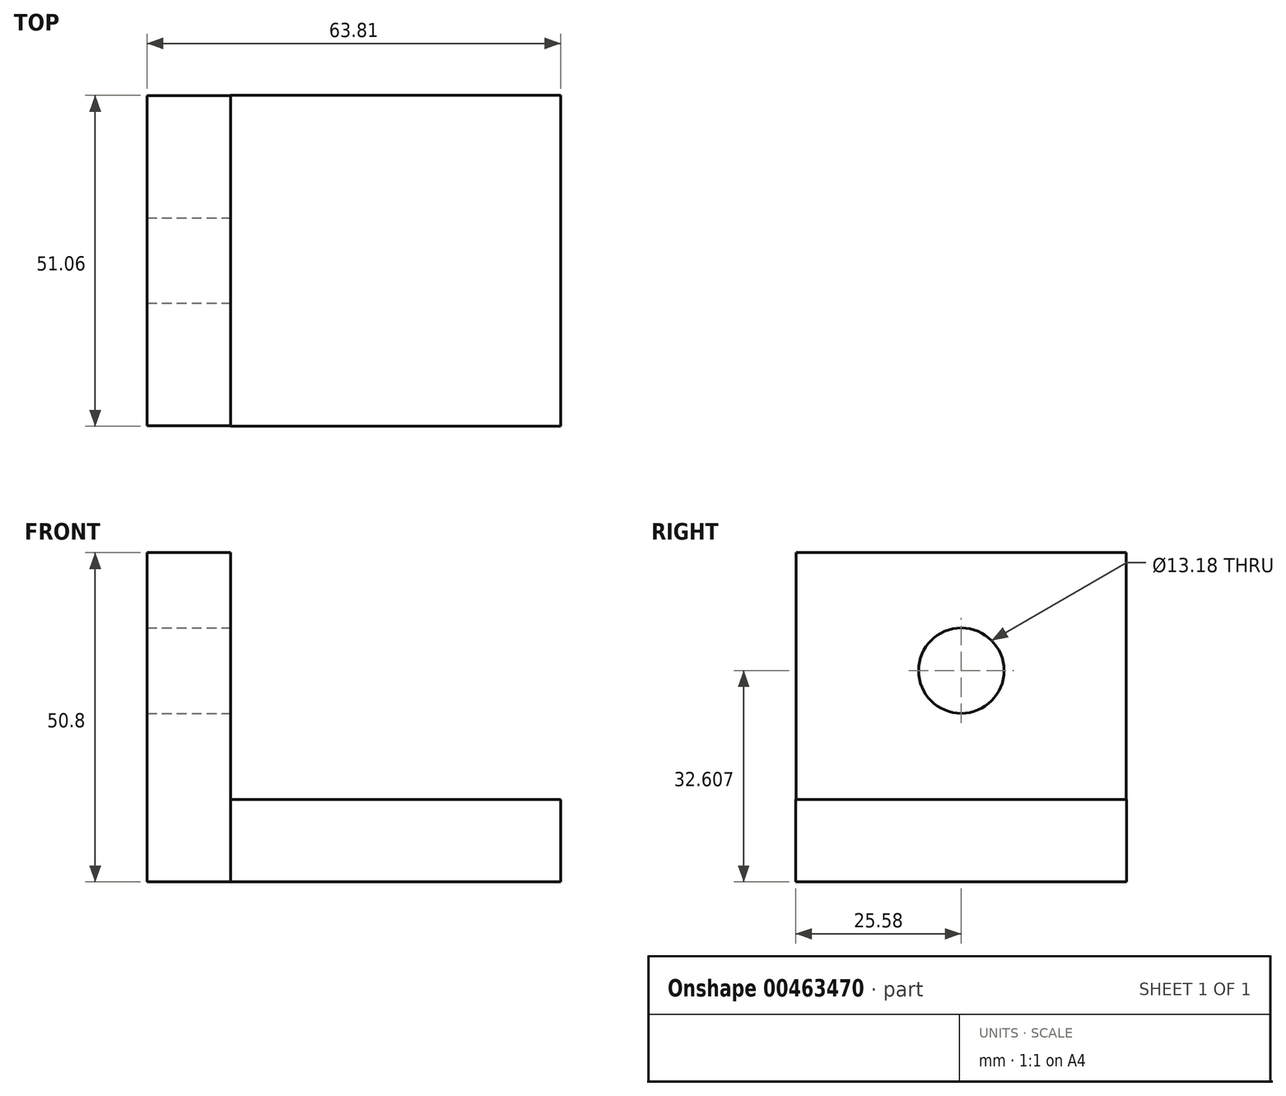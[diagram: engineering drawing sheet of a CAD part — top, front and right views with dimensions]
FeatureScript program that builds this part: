
annotation { "Feature Type Name" : "Feature", "Feature Type Description" : "" }
export const myFeature = defineFeature(function(context is Context, id is Id, definition is map)
    precondition{}
    {
        {
            var Q0;
            Q0=qCreatedBy(makeId("Top.planeOp"),FACE);
            var sketch = newSketch(context, id + "F0", { "sketchPlane" : qUnion([Q0])});
            skLineSegment(sketch, "E0", {"start": v(0, 0) * mm, "end": v(0, 25.48) * mm});
            skLineSegment(sketch, "E1", {"start": v(0, 25.48) * mm, "end": v(50.95, 25.48) * mm});
            skLineSegment(sketch, "E2", {"start": v(50.95, 25.48) * mm, "end": v(50.95, -25.58) * mm});
            skLineSegment(sketch, "E3", {"start": v(50.95, -25.58) * mm, "end": v(0, -25.58) * mm});
            skLineSegment(sketch, "E4", {"start": v(0, -25.58) * mm, "end": v(0, 0) * mm});
            skSolve(sketch);
        }
        {
            var Q0;
            Q0=qCreatedBy(makeId("Top.planeOp"),FACE);
            var sketch = newSketch(context, id + "F1", { "sketchPlane" : qUnion([Q0])});
            skLineSegment(sketch, "E5", {"start": v(0, -25.48) * mm, "end": v(-12.86, -25.48) * mm});
            skLineSegment(sketch, "E6", {"start": v(-12.86, -25.48) * mm, "end": v(-12.86, 25.42) * mm});
            skLineSegment(sketch, "E7", {"start": v(-12.86, 25.42) * mm, "end": v(0, 25.42) * mm});
            skLineSegment(sketch, "E8", {"start": v(0, 25.42) * mm, "end": v(0, -25.48) * mm});
            skSolve(sketch);
        }
        {
            var Q0;
            Q0=makeQuery(id+"F0.imprint","IMPRINT",FACE,{"disambiguationData":[TD([[makeQuery(id+"F0.imprint","IMPRINT",EDGE,{"derivedFrom":sQuery(id+"F0.wireOp",EDGE,"E0")}),-1.0]])]});
            extrude(context, id + "F2", {"entities" : qUnion([Q0]), "depth" : 12.7 * mm});
        }
        {
            var Q0;
            Q0=makeQuery(id+"F1.imprint","IMPRINT",FACE,{"disambiguationData":[TD([[makeQuery(id+"F1.imprint","IMPRINT",EDGE,{"derivedFrom":sQuery(id+"F1.wireOp",EDGE,"E5")}),-1.0]])]});
            extrude(context, id + "F3", {"entities" : qUnion([Q0]), "operationType" : NewBodyOperationType.ADD, "depth" : 50.8 * mm});
        }
        {
            var Q0;
            Q0=makeQuery(id+"F3.opExtrude","SWEPT_FACE",FACE,{"disambiguationData":[OSD([sQuery(id+"F1.wireOp",EDGE,"E8")])]});
            var sketch = newSketch(context, id + "F4", { "sketchPlane" : qUnion([Q0])});
            skCircle(sketch, "E9", {"center": v(0, 32.6) * mm, "radius": 6.59 * mm});
            skSolve(sketch);
        }
        {
            var Q0;
            Q0=makeQuery(id+"F4.imprint","IMPRINT",FACE,{"disambiguationData":[TD([[makeQuery(id+"F4.imprint","IMPRINT",EDGE,{"derivedFrom":sQuery(id+"F4.wireOp",EDGE,"E9")}),1.0]])]});
            extrude(context, id + "F5", {"entities" : qUnion([Q0]), "operationType" : NewBodyOperationType.REMOVE, "oppositeDirection" : true, "depth" : 41.66 * mm});
        }
    });
